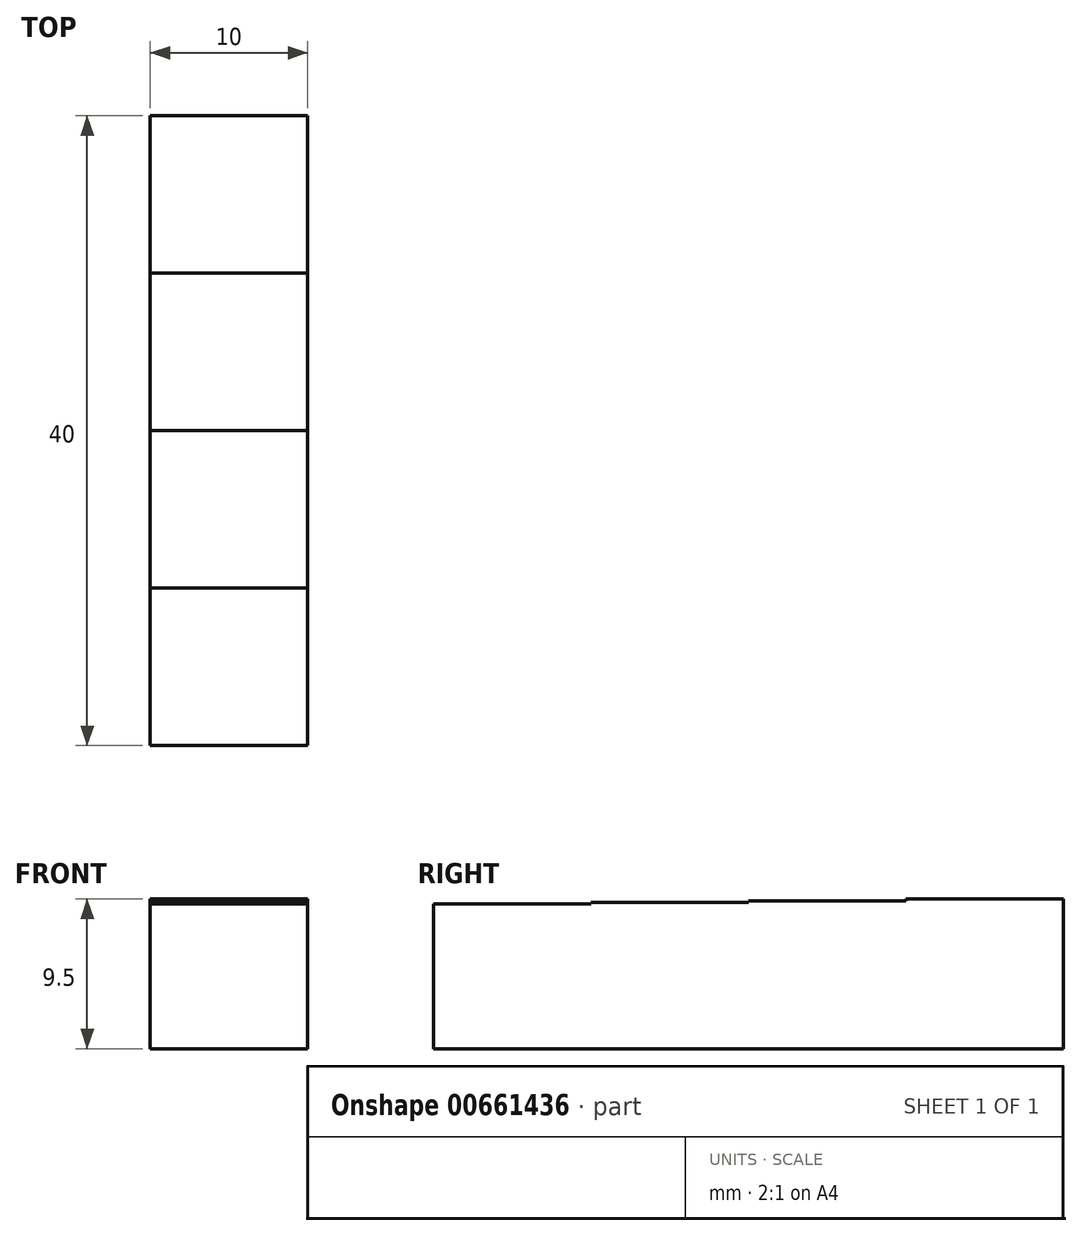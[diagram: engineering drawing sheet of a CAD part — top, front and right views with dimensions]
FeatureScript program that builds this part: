
annotation { "Feature Type Name" : "Feature", "Feature Type Description" : "" }
export const myFeature = defineFeature(function(context is Context, id is Id, definition is map)
    precondition{}
    {
        {
            var Q0;
            Q0=qCreatedBy(makeId("Right.planeOp"),FACE);
            var sketch = newSketch(context, id + "F0", { "sketchPlane" : qUnion([Q0])});
            skLineSegment(sketch, "E0", {"start": v(0, 0) * mm, "end": v(0, 9.2) * mm});
            skLineSegment(sketch, "E1", {"start": v(0, 9.2) * mm, "end": v(10, 9.2) * mm});
            skLineSegment(sketch, "E2", {"start": v(10, 9.2) * mm, "end": v(10, 9.3) * mm});
            skLineSegment(sketch, "E3", {"start": v(10, 9.3) * mm, "end": v(20, 9.3) * mm});
            skLineSegment(sketch, "E4", {"start": v(20, 9.3) * mm, "end": v(20, 9.4) * mm});
            skLineSegment(sketch, "E5", {"start": v(20, 9.4) * mm, "end": v(30, 9.4) * mm});
            skLineSegment(sketch, "E6", {"start": v(30, 9.4) * mm, "end": v(30, 9.5) * mm});
            skLineSegment(sketch, "E7", {"start": v(30, 9.5) * mm, "end": v(40, 9.5) * mm});
            skLineSegment(sketch, "E8", {"start": v(40, 9.5) * mm, "end": v(40, 0) * mm});
            skLineSegment(sketch, "E9", {"start": v(40, 0) * mm, "end": v(0, 0) * mm});
            skSolve(sketch);
        }
        {
            var Q0;
            Q0 = qSketchRegion(id + "F0", true);
            extrude(context, id + "F1", {"entities" : qUnion([Q0]), "depth" : 10 * mm, "offsetDistance" : 25 * mm});
        }
    });
